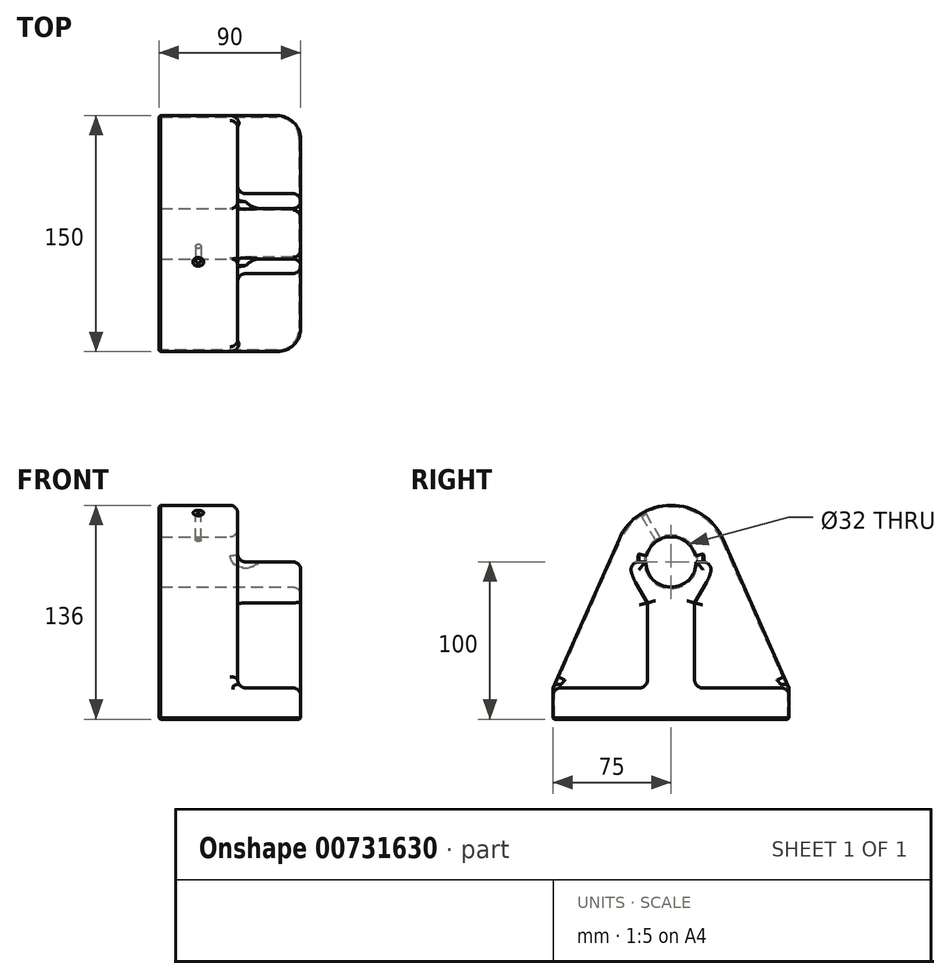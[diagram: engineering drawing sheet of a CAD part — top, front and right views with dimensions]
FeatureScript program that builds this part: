
annotation { "Feature Type Name" : "Feature", "Feature Type Description" : "" }
export const myFeature = defineFeature(function(context is Context, id is Id, definition is map)
    precondition{}
    {
        {
            assignVariable(context, id + "F0", {"name" : "Outer_Wall", "anyValue" : 20});
        }
        {
            assignVariable(context, id + "F1", {"name" : "Upstand_Length", "anyValue" : 50});
        }
        {
            assignVariable(context, id + "F2", {"name" : "Base_Add_Length", "anyValue" : 40});
        }
        {
            var Q0;
            Q0=qCreatedBy(makeId("Right.planeOp"),FACE);
            var sketch = newSketch(context, id + "F3", { "sketchPlane" : qUnion([Q0])});
            skCircle(sketch, "E0", {"center": v(0, 100) * mm, "radius": 16 * mm});
            skCircle(sketch, "E1", {"center": v(0, 100) * mm, "radius": 36 * mm});
            skLineSegment(sketch, "E2", {"start": v(-75, 0) * mm, "end": v(75, 0) * mm});
            skLineSegment(sketch, "E3", {"start": v(75, 0) * mm, "end": v(75, 20) * mm});
            skLineSegment(sketch, "E4", {"start": v(75, 20) * mm, "end": v(32.9, 114.64) * mm});
            skLineSegment(sketch, "E5.MirrorCS", {"start": v(-75, 0) * mm, "end": v(-75, 20) * mm});
            skLineSegment(sketch, "E6.MirrorCS", {"start": v(-75, 20) * mm, "end": v(-32.9, 114.64) * mm});
            skSolve(sketch);
        }
        {
            var Q0;
            Q0 = qSketchRegion(id + "F3", true);
            extrude(context, id + "F4", {"entities" : qUnion([Q0]), "endBound" : BoundingType.SYMMETRIC, "oppositeDirection" : true, "depth" : (getVariable(context, 'Upstand_Length')) * mm, "offsetDistance" : 25 * mm});
        }
        {
            var Q0;
            Q0=makeQuery(id+"F4.opExtrude","CAP_FACE",FACE,{"disambiguationData":[OSD([sQuery(id+"F3.wireOp",EDGE,"E0"),sQuery(id+"F3.wireOp",EDGE,"E1"),sQuery(id+"F3.wireOp",EDGE,"E2"),sQuery(id+"F3.wireOp",EDGE,"E3"),sQuery(id+"F3.wireOp",EDGE,"E4"),sQuery(id+"F3.wireOp",EDGE,"E5.MirrorCS"),sQuery(id+"F3.wireOp",EDGE,"E6.MirrorCS")])],"isStart":true});
            var sketch = newSketch(context, id + "F5", { "sketchPlane" : qUnion([Q0])});
            skLineSegment(sketch, "E7.bottom", {"start": v(-75, 20) * mm, "end": v(75, 20) * mm});
            skLineSegment(sketch, "E7.top", {"start": v(-75, 0) * mm, "end": v(75, 0) * mm});
            skLineSegment(sketch, "E7.left", {"start": v(-75, 20) * mm, "end": v(-75, 0) * mm});
            skLineSegment(sketch, "E7.right", {"start": v(75, 20) * mm, "end": v(75, 0) * mm});
            skSolve(sketch);
        }
        {
            var Q0;
            Q0 = qSketchRegion(id + "F5", true);
            extrude(context, id + "F6", {"entities" : qUnion([Q0]), "operationType" : NewBodyOperationType.ADD, "depth" : (getVariable(context, 'Base_Add_Length')) * mm, "offsetDistance" : 25 * mm});
        }
        {
            var Q0;
            Q0=makeQuery(id+"F4.opExtrude","CAP_FACE",FACE,{"disambiguationData":[OSD([sQuery(id+"F3.wireOp",EDGE,"E0"),sQuery(id+"F3.wireOp",EDGE,"E1"),sQuery(id+"F3.wireOp",EDGE,"E2"),sQuery(id+"F3.wireOp",EDGE,"E3"),sQuery(id+"F3.wireOp",EDGE,"E4"),sQuery(id+"F3.wireOp",EDGE,"E5.MirrorCS"),sQuery(id+"F3.wireOp",EDGE,"E6.MirrorCS")])],"isStart":true});
            var sketch = newSketch(context, id + "F7", { "sketchPlane" : qUnion([Q0])});
            skLineSegment(sketch, "E8.0.0", {"start": v(-32.9, 114.64) * mm, "end": v(-75, 20) * mm});
            skLineSegment(sketch, "E8.0.1", {"start": v(-75, 20) * mm, "end": v(75, 20) * mm});
            skLineSegment(sketch, "E8.0.2", {"start": v(75, 20) * mm, "end": v(32.9, 114.64) * mm});
            skArc(sketch, "E8.0.3", {"start": v(32.9, 114.64) * mm, "mid": v(0, 136) * mm, "end": v(-32.9, 114.64) * mm});
            skCircle(sketch, "E9.0", {"center": v(0, 100) * mm, "radius": 26 * mm});
            skLineSegment(sketch, "E10", {"start": v(-26, 100) * mm, "end": v(-16, 100) * mm});
            skLineSegment(sketch, "E11", {"start": v(26, 100) * mm, "end": v(16, 100) * mm});
            skLineSegment(sketch, "E12", {"start": v(-15, 78.76) * mm, "end": v(-15, 20) * mm});
            skLineSegment(sketch, "E13", {"start": v(-15, 73.98) * mm, "end": v(-22.52, 87) * mm});
            skLineSegment(sketch, "E14.MirrorCS", {"start": v(15, 73.98) * mm, "end": v(22.52, 87) * mm});
            skLineSegment(sketch, "E15.MirrorCS", {"start": v(15, 78.76) * mm, "end": v(15, 20) * mm});
            skSolve(sketch);
        }
        {
            var Q0;
            {var subQ3=sQuery(id+"F7.wireOp",EDGE,"E10");Q0=makeQuery(id+"F7.imprint","IMPRINT",FACE,{"disambiguationData":[TD([[makeQuery(id+"F7.imprint","IMPRINT",EDGE,{"derivedFrom":subQ3}),-1.0]])]});}
            var Q1;
            {var subQ0=sQuery(id+"F7.wireOp",EDGE,"E14.MirrorCS");Q1=makeQuery(id+"F7.imprint","IMPRINT",FACE,{"disambiguationData":[TD([[makeQuery(id+"F7.imprint","IMPRINT",EDGE,{"derivedFrom":subQ0}),1.0]])]});}
            var Q2;
            {var subQ3=sQuery(id+"F7.wireOp",EDGE,"E13");Q2=makeQuery(id+"F7.imprint","IMPRINT",FACE,{"disambiguationData":[TD([[makeQuery(id+"F7.imprint","IMPRINT",EDGE,{"derivedFrom":subQ3}),-1.0]])]});}
            var Q3;
            {var subQ0=sQuery(id+"F7.wireOp",EDGE,"E12");var subQ1=sQuery(id+"F7.wireOp",EDGE,"E8.0.1");var subQ2=makeQuery(id+"F7.imprint","INTERSECT",VERTEX,{"derivedFrom":[subQ1,subQ0]});Q3=makeQuery(id+"F7.imprint","IMPRINT",FACE,{"disambiguationData":[TD([[makeQuery(id+"F7.imprint","IMPRINT",EDGE,{"disambiguationData":[TD([[subQ2,-1.0]])],"derivedFrom":subQ1}),1.0]])]});}
            extrude(context, id + "F8", {"entities" : qUnion([Q0, Q1, Q2, Q3]), "operationType" : NewBodyOperationType.ADD, "depth" : (getVariable(context, 'Base_Add_Length')) * mm, "offsetDistance" : 25 * mm});
        }
        {
            var Q0;
            Q0=makeQuery(id+"F4aXAo5B7PqX89m_1.1.F6.opExtrude","CAP_EDGE",EDGE,{"disambiguationData":[OSD([sQuery(id+"F5.wireOp",EDGE,"E7.left")])],"isStart":false});
            var Q1;
            Q1=makeQuery(id+"F6.opExtrude","CAP_EDGE",EDGE,{"disambiguationData":[OSD([sQuery(id+"F5.wireOp",EDGE,"E7.left")])],"isStart":false});
            var Q2;
            Q2=makeQuery(id+"F6.opExtrude","CAP_EDGE",EDGE,{"disambiguationData":[OSD([sQuery(id+"F5.wireOp",EDGE,"E7.right")])],"isStart":false});
            var Q3;
            Q3=makeQuery(id+"F4aXAo5B7PqX89m_1.1.F6.opExtrude","CAP_EDGE",EDGE,{"disambiguationData":[OSD([sQuery(id+"F5.wireOp",EDGE,"E7.right")])],"isStart":false});
            fillet(context, id + "F9", {"entities" : qUnion([Q0, Q1, Q2, Q3]), "radius" : 15 * mm, "tangentPropagation" : true, "allowEdgeOverflow" : false});
        }
        {
            var Q0;
            Q0=makeQuery(id+"F8.opExtrude","CAP_EDGE",EDGE,{"disambiguationData":[OSD([sQuery(id+"F7.wireOp",EDGE,"E12")])],"isStart":false});
            var Q1;
            Q1=makeQuery(id+"F8.opExtrude","CAP_EDGE",EDGE,{"disambiguationData":[OSD([sQuery(id+"F7.wireOp",EDGE,"E15.MirrorCS")])],"isStart":false});
            var Q2;
            Q2=makeQuery(id+"F8.opExtrude","CAP_EDGE",EDGE,{"disambiguationData":[OSD([sQuery(id+"F7.wireOp",EDGE,"E13")])],"isStart":false});
            var Q3;
            {var subQ0=sQuery(id+"F7.wireOp",EDGE,"E9.0");Q3=makeQuery(id+"F8.opExtrude","CAP_EDGE",EDGE,{"disambiguationData":[OSD([subQ0]),TDD([makeQuery(id+"F7.imprint","IMPRINT",EDGE,{"disambiguationData":[TD([[makeQuery(id+"F7.imprint","INTERSECT",VERTEX,{"derivedFrom":[subQ0,sQuery(id+"F7.wireOp",EDGE,"E10")]}),-1.0]])],"derivedFrom":subQ0})])],"isStart":false});}
            var Q4;
            Q4=makeQuery(id+"F8.opExtrude","CAP_EDGE",EDGE,{"disambiguationData":[OSD([sQuery(id+"F7.wireOp",EDGE,"E10")])],"isStart":false});
            var Q5;
            Q5=makeQuery(id+"F8.opExtrude","CAP_EDGE",EDGE,{"disambiguationData":[OSD([sQuery(id+"F3.wireOp",EDGE,"E0")])],"isStart":false});
            var Q6;
            Q6=makeQuery(id+"F8.opExtrude","CAP_EDGE",EDGE,{"disambiguationData":[OSD([sQuery(id+"F7.wireOp",EDGE,"E11")])],"isStart":false});
            var Q7;
            {var subQ0=sQuery(id+"F7.wireOp",EDGE,"E9.0");Q7=makeQuery(id+"F8.opExtrude","CAP_EDGE",EDGE,{"disambiguationData":[OSD([subQ0]),TDD([makeQuery(id+"F7.imprint","IMPRINT",EDGE,{"disambiguationData":[TD([[makeQuery(id+"F7.imprint","INTERSECT",VERTEX,{"derivedFrom":[subQ0,sQuery(id+"F7.wireOp",EDGE,"E11")]}),1.0]])],"derivedFrom":subQ0})])],"isStart":false});}
            var Q8;
            Q8=makeQuery(id+"F8.opExtrude","CAP_EDGE",EDGE,{"disambiguationData":[OSD([sQuery(id+"F7.wireOp",EDGE,"E14.MirrorCS")])],"isStart":false});
            var Q9;
            {var subQ1=sQuery(id+"F5.wireOp",EDGE,"E7.bottom");var subQ2=sQuery(id+"F3.wireOp",EDGE,"E3");Q9=makeQuery(id+"F8.boolean.opBoolean","SPLIT",FACE,{"disambiguationData":[TD([makeQuery(id+"F4.opExtrude","SWEPT_FACE",FACE,{"disambiguationData":[OSD([subQ2])]})])],"derivedFrom":makeQuery(id+"F6.opExtrude","SWEPT_FACE",FACE,{"disambiguationData":[OSD([subQ1])]})});}
            var Q10;
            {var subQ1=sQuery(id+"F5.wireOp",EDGE,"E7.bottom");var subQ5=sQuery(id+"F3.wireOp",EDGE,"E5.MirrorCS");Q10=makeQuery(id+"F8.boolean.opBoolean","SPLIT",FACE,{"disambiguationData":[TD([makeQuery(id+"F4.opExtrude","SWEPT_FACE",FACE,{"disambiguationData":[OSD([subQ5])]})])],"derivedFrom":makeQuery(id+"F6.opExtrude","SWEPT_FACE",FACE,{"disambiguationData":[OSD([subQ1])]})});}
            var Q11;
            Q11=makeQuery(id+"F4.opExtrude","CAP_FACE",FACE,{"disambiguationData":[OSD([sQuery(id+"F3.wireOp",EDGE,"E0"),sQuery(id+"F3.wireOp",EDGE,"E1"),sQuery(id+"F3.wireOp",EDGE,"E2"),sQuery(id+"F3.wireOp",EDGE,"E3"),sQuery(id+"F3.wireOp",EDGE,"E4"),sQuery(id+"F3.wireOp",EDGE,"E5.MirrorCS"),sQuery(id+"F3.wireOp",EDGE,"E6.MirrorCS")])],"isStart":true});
            var Q12;
            Q12=makeQuery(id+"F8.opExtrude","SWEPT_EDGE",EDGE,{"disambiguationData":[OSD([sQuery(id+"F7.wireOp",EDGE,"E9.0"),sQuery(id+"F7.wireOp",EDGE,"E10")])]});
            var Q13;
            Q13=makeQuery(id+"F8.opExtrude","SWEPT_EDGE",EDGE,{"disambiguationData":[OSD([sQuery(id+"F7.wireOp",EDGE,"E9.0"),sQuery(id+"F7.wireOp",EDGE,"E11")])]});
            var Q14;
            Q14=makeQuery(id+"F4.opExtrude","SWEPT_EDGE",EDGE,{"disambiguationData":[OSD([sQuery(id+"F3.wireOp",EDGE,"E5.MirrorCS"),sQuery(id+"F3.wireOp",EDGE,"E6.MirrorCS")])]});
            fillet(context, id + "F10", {"entities" : qUnion([Q0, Q1, Q2, Q3, Q4, Q5, Q6, Q7, Q8, Q9, Q10, Q11, Q12, Q13, Q14]), "radius" : 5 * mm, "tangentPropagation" : true, "allowEdgeOverflow" : false});
        }
        {
            var Q0;
            Q0=makeQuery(id+"F4.opExtrude","CAP_FACE",FACE,{"disambiguationData":[OSD([sQuery(id+"F3.wireOp",EDGE,"E0"),sQuery(id+"F3.wireOp",EDGE,"E1"),sQuery(id+"F3.wireOp",EDGE,"E2"),sQuery(id+"F3.wireOp",EDGE,"E3"),sQuery(id+"F3.wireOp",EDGE,"E4"),sQuery(id+"F3.wireOp",EDGE,"E5.MirrorCS"),sQuery(id+"F3.wireOp",EDGE,"E6.MirrorCS")])],"isStart":false});
            var Q1;
            Q1=makeQuery(id+"F6.boolean.opBoolean","MERGE",FACE,{"derivedFrom":[makeQuery(id+"F4.opExtrude","SWEPT_FACE",FACE,{"disambiguationData":[OSD([sQuery(id+"F3.wireOp",EDGE,"E2")])]}),makeQuery(id+"F6.opExtrude","SWEPT_FACE",FACE,{"disambiguationData":[OSD([sQuery(id+"F5.wireOp",EDGE,"E7.top")])]})]});
            chamfer(context, id + "F11", {"entities" : qUnion([Q0, Q1]), "width" : 1 * mm, "tangentPropagation" : true});
        }
        {
            var Q0;
            Q0=qCreatedBy(makeId("Right.planeOp"),FACE);
            var sketch = newSketch(context, id + "F12", { "sketchPlane" : qUnion([Q0])});
            skArc(sketch, "E16.0", {"start": v(15.54, 103.8) * mm, "mid": v(0, 116) * mm, "end": v(-15.54, 103.8) * mm});
            skLineSegment(sketch, "E17", {"start": v(0, 100) * mm, "end": v(-18, 131.18) * mm, "construction": true});
            skSolve(sketch);
        }
        {
            var Q0;
            Q0=sQuery(id+"F12.wireOp",VERTEX,"E17.end");
            var Q1;
            Q1=sQuery(id+"F12.wireOp",EDGE,"E17");
            cPlane(context, id + "F13", {"entities" : qUnion([Q0, Q1]), "cplaneType" : CPlaneType.LINE_POINT, "offset" : 25 * mm, "width" : 150 * mm, "height" : 150 * mm});
        }
        {
            var Q0;
            Q0=qCreatedBy(id+"F13.planeOp",FACE);
            var sketch = newSketch(context, id + "F14", { "sketchPlane" : qUnion([Q0])});
            skPoint(sketch, "E18.0", {"position": v(0, 50) * mm});
            skCircle(sketch, "E19", {"center": v(0, 50) * mm, "radius": 9.38 * mm});
            skSolve(sketch);
        }
        {
            var Q0;
            Q0=sQuery(id+"F14.wireOp",VERTEX,"E18.0");
            var Q1;
            Q1=makeQuery(id+"F4.opExtrude","SWEPT_BODY",BODY,{"disambiguationData":[OSD([sQuery(id+"F3.wireOp",EDGE,"E0"),sQuery(id+"F3.wireOp",EDGE,"E1"),sQuery(id+"F3.wireOp",EDGE,"E2"),sQuery(id+"F3.wireOp",EDGE,"E3"),sQuery(id+"F3.wireOp",EDGE,"E4"),sQuery(id+"F3.wireOp",EDGE,"E5.MirrorCS"),sQuery(id+"F3.wireOp",EDGE,"E6.MirrorCS")])]});
            hole(context, id + "F15", {"style" : HoleStyle.C_SINK, "endStyle" : HoleEndStyle.BLIND, "standardTappedOrClearance" : lookupTablePath({ "standard" : "ISO", "fit" : "Normal", "size" : "M3", "type" : "Clearance" }), "standardBlindInLast" : lookupTablePath({ "fit" : "Standard", "standard" : "ISO", "size" : "M3", "type" : "Clearance" }), "holeDiameter" : 3.3 * mm, "cSinkDiameter" : 6.72 * mm, "cSinkAngle" : 90 * degree, "majorDiameter" : 5 * mm, "holeDepth" : (getVariable(context, 'Outer_Wall') + 5) * mm, "isTappedThrough" : true, "tappedDepth" : 12 * mm, "tapClearance" : 3, "startFromSketch" : true, "locations" : qUnion([Q0]), "scope" : qUnion([Q1])});
        }
    });
